# Revit family: MDW
name_source: partatom
category: Generic Models
units: mm (PartAtom-declared; Revit-internal decimal feet)

## family parameters
Can host rebar = No
Cut with Voids When Loaded = No
Host = Face
Maintain Annotation Orientation = No
Part Type = Normal
Room Calculation Point = No
Round Connector Dimension = Use Diameter
Shared = No

## types (11) — shared parameters
Default Elevation = 4' - 0"
Description = DRYWALL BEAD ACCESS DOOR
Manufacturer = MIFAB
Material = <By Category>
Model = MDW
URL = WWW.MIFAB.COM

## per-type parameters (varying)
| type | Height | Width |
| MDW-8"8" | 0' - 8" | 0' - 8" |
| MDW-10"x10" | 0' - 10" | 0' - 10" |
| MDW-12"x12" | 1' - 0" | 1' - 0" |
| MDW-14"x14" | 1' - 2" | 1' - 2" |
| MDW-16"x16" | 1' - 4" | 1' - 4" |
| MDW-18"x18" | 1' - 6" | 1' - 6" |
| MDW-22"x22" | 1' - 10" | 1' - 10" |
| MDW-24"x24" | 2' - 0" | 2' - 0" |
| MDW-24"x36" | 3' - 0" | 2' - 0" |
| MDW-30"x30" | 2' - 6" | 2' - 6" |
| MDW-36"x36" | 3' - 0" | 3' - 0" |

## geometry (parser evidence)
native form markers: Sweep x5
no freeform markers — native parametric forms only
